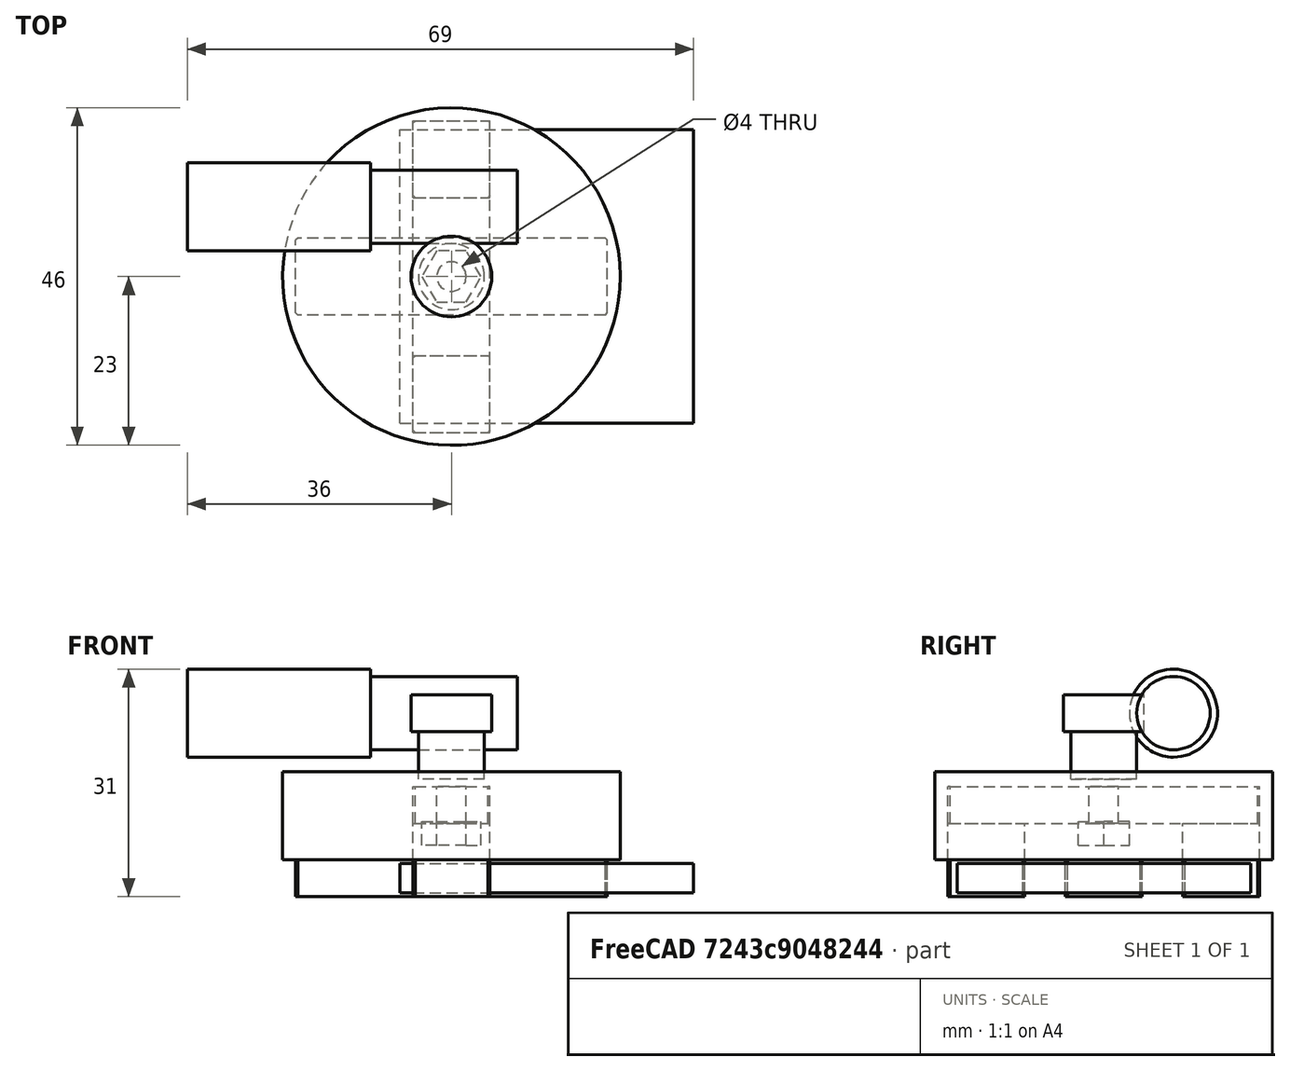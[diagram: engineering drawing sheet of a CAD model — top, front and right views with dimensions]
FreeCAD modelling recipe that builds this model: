
FCSTD DOCUMENT  (FreeCAD 0.18.4R)
Label: clamp
License: All rights reserved
LicenseURL: http://en.wikipedia.org/wiki/All_rights_reserved
objects: Part::Box×7, Part::Cylinder×6, Part::Chamfer×4, Part::Cut×1, Part::Feature×1, Part::MultiFuse×1
note: 20 computed .brp shape members not serialized (recipe doc carries the construction recipe); baked Part::Feature solids carry a one-line shape summary decoded from their .brp

FEATURE [Part::Box] Box004  label="square-magnet"
  AttacherType = Attacher::AttachEngine3D
  Height = 5
  Length = 10.5
  Placement = pos=(-5.25,10.75,5) rot=(0,0,1;0rad)
  Width = 10.5
FEATURE [Part::Box] Box005  label="Square Magnet001"
  AttacherType = Attacher::AttachEngine3D
  Height = 5
  Length = 10.5
  Placement = pos=(-5.25,-5.25,0) rot=(0,0,1;0rad)
  Width = 10.5
FEATURE [Part::Cylinder] Cylinder  label="centre"
  Angle = 360
  AttacherType = Attacher::AttachEngine3D
  Height = 12
  Placement = pos=(0,0,5) rot=(0,0,1;0rad)
  Radius = 23
FEATURE [Part::Chamfer] Chamfer  label="square-iron"
  Base = -> Box005
  Edges = 4 edges r=0.3: [Edge1,Edge3,Edge5,Edge7]
  Placement = pos=(0,16,0) rot=(0,0,1;0rad)
FEATURE [Part::Box] Box009  label="square-magnet001"
  AttacherType = Attacher::AttachEngine3D
  Height = 5
  Length = 10.5
  Placement = pos=(-5.25,-21.25,5) rot=(0,0,1;0rad)
  Width = 10.5
FEATURE [Part::Box] Box010  label="rectangular-iron002"
  AttacherType = Attacher::AttachEngine3D
  Height = 5
  Length = 10.5
  Placement = pos=(-5.25,-21.25,0) rot=(0,0,1;0rad)
  Width = 42.5
FEATURE [Part::Box] Box  label="Cube"
  AttacherType = Attacher::AttachEngine3D
  Height = 4
  Length = 40
  Placement = pos=(-7,-20,0.5) rot=(0,0,1;0rad)
  Width = 40
FEATURE [Part::Box] Box011  label="Square Magnet002"
  AttacherType = Attacher::AttachEngine3D
  Height = 5
  Length = 10.5
  Placement = pos=(-5.25,-5.25,0) rot=(0,0,1;0rad)
  Width = 10.5
FEATURE [Part::Chamfer] Chamfer003  label="square-iron001"
  Base = -> Box011
  Edges = 4 edges r=0.3: [Edge1,Edge3,Edge5,Edge7]
  Placement = pos=(0,-16,0) rot=(0,0,1;0rad)
FEATURE [Part::Chamfer] Chamfer004  label="rectangular-iron"
  Base = -> Box010
  Edges = 4 edges r=0.3: [Edge1,Edge3,Edge5,Edge7]
  Placement = pos=(0,0,0) rot=(0,0,1;1.5708rad)
FEATURE [Part::Box] Box012  label="rectangular-iron003"
  AttacherType = Attacher::AttachEngine3D
  Height = 5
  Length = 10.5
  Placement = pos=(-5.25,-21.25,0) rot=(0,0,1;0rad)
  Width = 42.5
FEATURE [Part::Chamfer] Chamfer005  label="keeper-a"
  Base = -> Box012
  Edges = 4 edges r=0.3: [Edge1,Edge3,Edge5,Edge7]
  Placement = pos=(0,0,10) rot=(0,0,1;0rad)
FEATURE [Part::Cylinder] Cylinder001  label="M4-tap"
  Angle = 360
  AttacherType = Attacher::AttachEngine3D
  Height = 12
  Placement = pos=(0,0,5) rot=(0,0,1;0rad)
  Radius = 2
FEATURE [Part::Cut] Cut
  Base = -> Chamfer005
  Tool = -> Cylinder001
FEATURE [Part::Feature] Shape  label="M4-nut"
  Placement = pos=(0,0,7) rot=(0,0,1;0rad)
  shape: bbox 8.083 x 7 x 3.25 mm, 8 faces (baked)
FEATURE [Part::Cylinder] Cylinder002  label="centre001"
  Angle = 360
  AttacherType = Attacher::AttachEngine3D
  Height = 6.6
  Placement = pos=(0,0,-9) rot=(0,0,1;0rad)
  Radius = 4.5
FEATURE [Part::Cylinder] Cylinder003  label="centre002"
  Angle = 360
  AttacherType = Attacher::AttachEngine3D
  Height = 5
  Placement = pos=(0,0,-2.5) rot=(0,0,1;0rad)
  Radius = 5.5
FEATURE [Part::Cylinder] Cylinder004  label="worm-drive-gear"
  Angle = 360
  AttacherType = Attacher::AttachEngine3D
  Height = 20
  Placement = pos=(-11,9.5,25) rot=(0,1,0;1.5708rad)
  Radius = 5
FEATURE [Part::MultiFuse] Fusion  label="worm-driven-gear"
  Placement = pos=(0,0,25) rot=(0,0,1;0rad)
  Shapes = -> [Cylinder002,Cylinder003]
FEATURE [Part::Cylinder] Cylinder005  label="motor-1"
  Angle = 360
  AttacherType = Attacher::AttachEngine3D
  Height = 25
  Placement = pos=(-36,9.5,25) rot=(0,1,0;1.5708rad)
  Radius = 6
